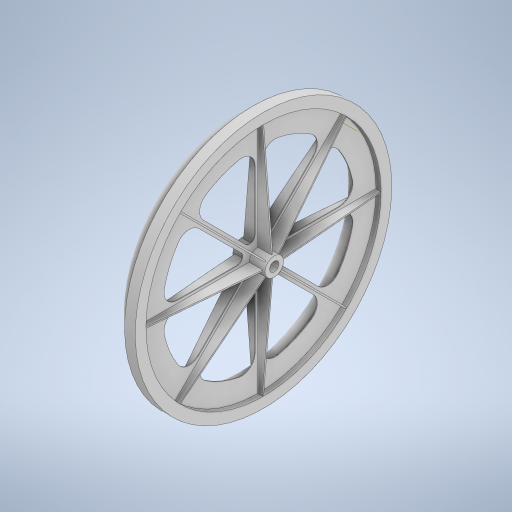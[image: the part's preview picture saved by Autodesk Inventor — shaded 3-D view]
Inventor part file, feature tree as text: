
AUTODESK INVENTOR PART (.ipt)
format: ipt  version: 2023 (Build 270158000, 158)  size: 518,144 bytes
history: native  units: in
note: dims shown in document units (in); Inventor stores cm internally (conversion verified against a paired STEP export)
features: sketch x10, extrude x6, other x4, plane x2, loft x1, pattern_circular x1, revolve x1
ambient origin geometry x8: Origin, YZ Plane, XZ Plane, XY Plane, X Axis, Y Axis, Z Axis, Center Point
bodies: Solid1 (feature_tree)
feature tree (25):
  extrude  "Extrusion1"  Depth=1.5in TaperAngle=0.0deg
  extrude  "Extrusion2"  Depth=0.03in TaperAngle=0.0deg
  extrude  "Extrusion3"  Depth=0.5in TaperAngle=0.0deg
  extrude  "Extrusion4"  Depth=2.0in
  plane  "Work Plane1"
  loft  "Loft1"
  other  "Work Axis1"
  extrude  "Extrusion5"  Depth=1.25in
  pattern_circular  "Circular Pattern1"  [2 undecoded]
  extrude  "Extrusion6"  Depth=0.125in
  plane  "Work Plane2"
  other  "Work Axis2"
  sketch  "Sketch9"  dims[d24=0.125in]
  other  "Work Axis3"
  sketch  "Sketch10"  dims[d25=0.125in d26=0.875in d27=0.125in d28=0.0in d29=90.0deg d30=0.0in d31=90.0deg d32=0.4375in d33=10.5in d34=1.125in d35=0.0in d36=3.1496in d37=360.0deg d39=0.875in d40=14.0625in d41=0.0in d42=0.75in d43=90.0deg]
  revolve  "Revolution1"  Angle=90.0deg
  sketch  "Sketch1"  dims[d0=1.75in d1=1.5in d2=1.5in d3=0.0in d4=0.0in]
  sketch  "Sketch2"  dims[d5=24.0in d6=0.03in d7=0.03in d8=0.0in d9=0.0in]
  sketch  "Sketch3"  dims[d10=1.0in d11=0.5in d12=0.5in d13=0.0in d14=0.0in]
  sketch  "Sketch4"  dims[d15=45.0deg d16=2.0in]
  sketch  "Sketch5"  dims[d17=0.625in d18=0.625in]
  sketch  "Sketch6"  dims[d19=0.5in d20=1.25in]
  sketch  "Sketch7"  dims[d21=6.5in d22=0.0in]
  sketch  "Sketch8"  dims[d23=11.1in]
  other  "Work Point1"
note: 2 required parameter values undecoded (feature->parameter linkage not recoverable at this tier; creation-order binding heuristic only, values carry confidence <= 0.55)
